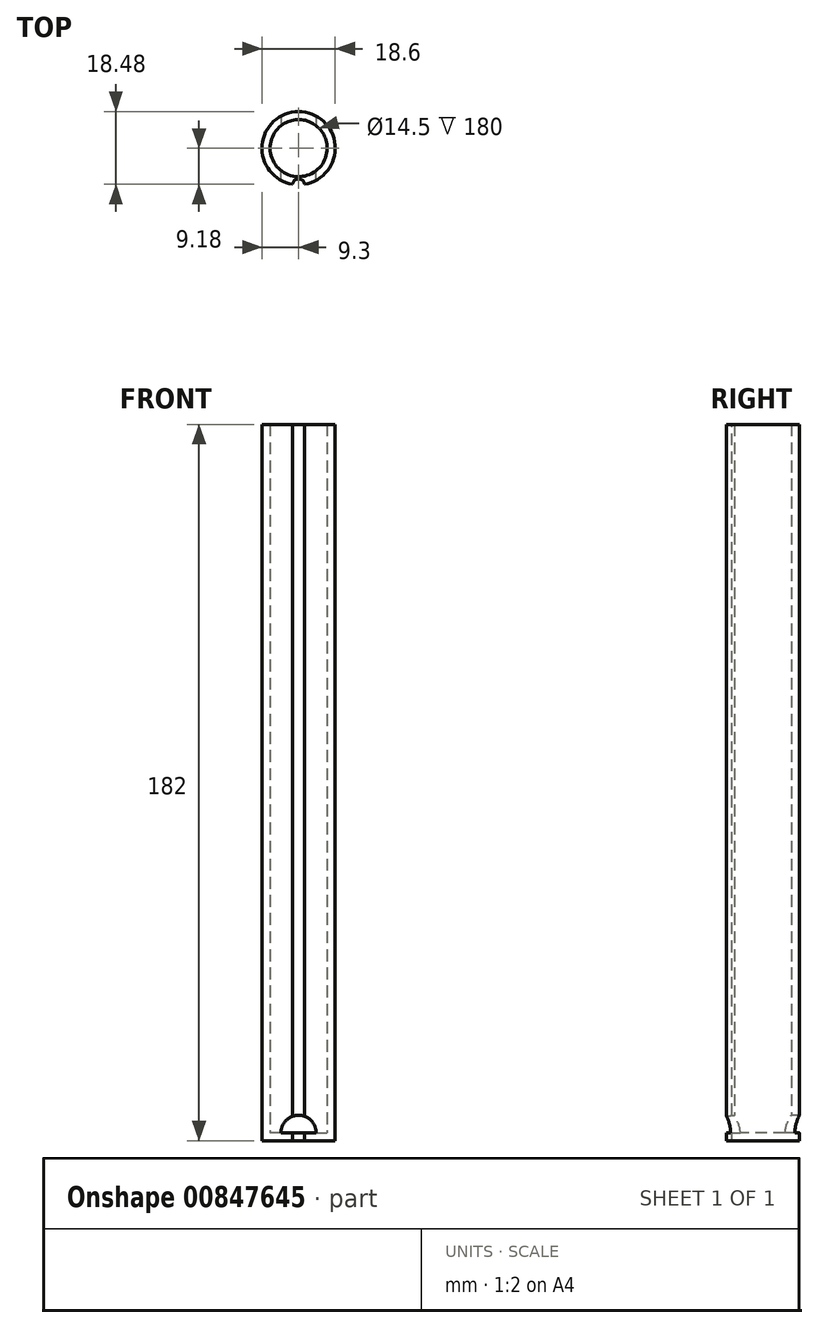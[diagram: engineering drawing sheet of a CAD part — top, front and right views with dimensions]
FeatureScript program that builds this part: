
annotation { "Feature Type Name" : "Feature", "Feature Type Description" : "" }
export const myFeature = defineFeature(function(context is Context, id is Id, definition is map)
    precondition{}
    {
        {
            var Q0;
            Q0=qCreatedBy(makeId("Top.planeOp"),FACE);
            var sketch = newSketch(context, id + "F0", { "sketchPlane" : qUnion([Q0])});
            skCircle(sketch, "E0", {"center": v(0, 0) * mm, "radius": 9.3 * mm});
            skSolve(sketch);
        }
        {
            var Q0;
            Q0=makeQuery(id+"F0.imprint","IMPRINT",FACE,{"disambiguationData":[TD([[makeQuery(id+"F0.imprint","IMPRINT",EDGE,{"derivedFrom":sQuery(id+"F0.wireOp",EDGE,"E0")}),1.0]])]});
            extrude(context, id + "F1", {"entities" : qUnion([Q0]), "depth" : 2 * mm, "offsetDistance" : 25 * mm});
        }
        {
            var Q0;
            Q0=makeQuery(id+"F1.opExtrude","CAP_FACE",FACE,{"disambiguationData":[OSD([sQuery(id+"F0.wireOp",EDGE,"E0")])],"isStart":false});
            var sketch = newSketch(context, id + "F2", { "sketchPlane" : qUnion([Q0])});
            skCircle(sketch, "E1", {"center": v(0, 0) * mm, "radius": 7.25 * mm});
            skSolve(sketch);
        }
        {
            var Q0;
            Q0=makeQuery(id+"F2.imprint","IMPRINT",FACE,{"disambiguationData":[TD([[makeQuery(id+"F2.imprint","IMPRINT",EDGE,{"derivedFrom":sQuery(id+"F2.wireOp",EDGE,"E1")}),-1.0]])]});
            extrude(context, id + "F3", {"entities" : qUnion([Q0]), "operationType" : NewBodyOperationType.ADD, "depth" : 180 * mm, "offsetDistance" : 25 * mm});
        }
        {
            var Q0;
            Q0=qCreatedBy(makeId("Front.planeOp"),FACE);
            var sketch = newSketch(context, id + "F4", { "sketchPlane" : qUnion([Q0])});
            skLineSegment(sketch, "E2", {"start": v(-9.74, 2) * mm, "end": v(11.68, 2) * mm});
            skArc(sketch, "E3", {"start": v(0, 6.47) * mm, "mid": v(-3.16, 5.16) * mm, "end": v(-4.47, 2) * mm});
            skArc(sketch, "E4", {"start": v(0, 6.47) * mm, "mid": v(3.16, 5.16) * mm, "end": v(4.47, 2) * mm});
            skSolve(sketch);
        }
        {
            var Q0;
            {var subQ0=sQuery(id+"F4.wireOp",EDGE,"E3");Q0=makeQuery(id+"F4.imprint","IMPRINT",FACE,{"disambiguationData":[TD([[makeQuery(id+"F4.imprint","IMPRINT",EDGE,{"derivedFrom":subQ0}),1.0]])]});}
            extrude(context, id + "F5", {"entities" : qUnion([Q0]), "operationType" : NewBodyOperationType.REMOVE, "endBound" : BoundingType.THROUGH_ALL, "oppositeDirection" : true, "depth" : 25 * mm, "offsetDistance" : 25 * mm});
        }
        {
            var Q0;
            {var subQ0=sQuery(id+"F4.wireOp",EDGE,"E3");Q0=makeQuery(id+"F4.imprint","IMPRINT",FACE,{"disambiguationData":[TD([[makeQuery(id+"F4.imprint","IMPRINT",EDGE,{"derivedFrom":subQ0}),1.0]])]});}
            extrude(context, id + "F6", {"entities" : qUnion([Q0]), "operationType" : NewBodyOperationType.REMOVE, "endBound" : BoundingType.THROUGH_ALL, "depth" : 25 * mm, "offsetDistance" : 25 * mm});
        }
        {
            var Q0;
            Q0=makeQuery(id+"F3.opExtrude","CAP_FACE",FACE,{"disambiguationData":[OSD([sQuery(id+"F0.wireOp",EDGE,"E0"),sQuery(id+"F2.wireOp",EDGE,"E1")])],"isStart":false});
            var sketch = newSketch(context, id + "F7", { "sketchPlane" : qUnion([Q0])});
            skCircle(sketch, "E5", {"center": v(0, -9.3) * mm, "radius": 1.5 * mm});
            skSolve(sketch);
        }
        {
            var Q0;
            {var subQ0=sQuery(id+"F7.wireOp",EDGE,"E5");var subQ1=makeQuery(id+"F3.opExtrude","CAP_EDGE",EDGE,{"disambiguationData":[OSD([sQuery(id+"F0.wireOp",EDGE,"E0")])],"isStart":false});var subQ2=makeQuery(id+"F7.imprint","INTERSECT",VERTEX,{"disambiguationData":[OD(0.0)],"derivedFrom":[subQ1,subQ0]});Q0=makeQuery(id+"F7.imprint","IMPRINT",FACE,{"disambiguationData":[TD([[makeQuery(id+"F7.imprint","IMPRINT",EDGE,{"disambiguationData":[TD([[subQ2,1.0]])],"derivedFrom":subQ0}),1.0]])]});}
            extrude(context, id + "F8", {"entities" : qUnion([Q0]), "operationType" : NewBodyOperationType.REMOVE, "endBound" : BoundingType.THROUGH_ALL, "oppositeDirection" : true, "depth" : 25 * mm, "offsetDistance" : 25 * mm});
        }
    });
